# Revit family: OvaLED NM ST LED 230V 1t (takmontasje)
name_source: partatom
category: Lighting Fixtures
revit_build: Autodesk Revit 2013 (Build: 20130531_2115(x64)
units: mm (PartAtom-declared; Revit-internal decimal feet)

## types (1)
- Type 1
    Color Filter = 16777215
    Dimming Lamp Color Temperature Shift = <None>
    Emit Shape Visible in Rendering = No
    Emit from Rectangle Length = 160 mm  [stored 0.524934 ft]
    Emit from Rectangle Width = 160 mm  [stored 0.524934 ft]
    Glass Material = Plastic - Glass
    Height = 55 mm  [stored 0.180446 ft]
    Height 1 = 45 mm
    Length A = 160 mm  [stored 0.524934 ft]
    Length B = 160 mm  [stored 0.524934 ft]
    Material = Plastic - White
    Number of Poles = 1
    Photometric Web File = 2x4 3Lamp.ies
    Tilt Angle = 90.00°
    Voltage = 230 V

note: [stored X ft] marks values corroborated as IEEE doubles in the binary element streams (Revit-internal decimal feet)

## geometry (parser evidence)
native form markers: Blend x2, Sweep x3
no freeform markers — native parametric forms only
